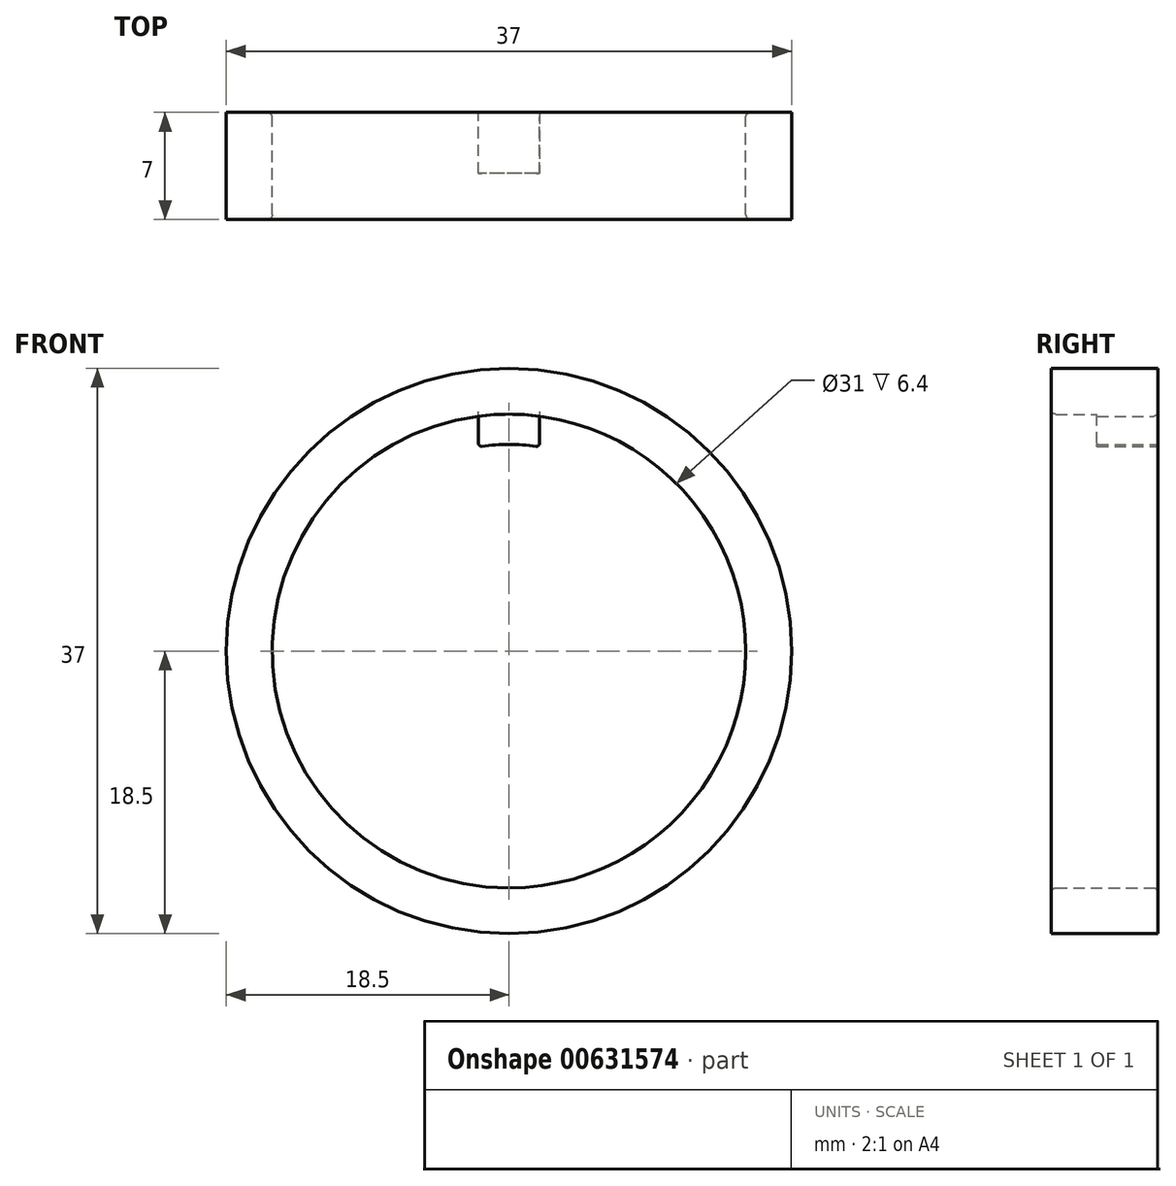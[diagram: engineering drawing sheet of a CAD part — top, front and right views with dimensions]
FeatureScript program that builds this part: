
annotation { "Feature Type Name" : "Feature", "Feature Type Description" : "" }
export const myFeature = defineFeature(function(context is Context, id is Id, definition is map)
    precondition{}
    {
        {
            var Q0;
            Q0=qCreatedBy(makeId("Front.planeOp"),FACE);
            var sketch = newSketch(context, id + "F0", { "sketchPlane" : qUnion([Q0])});
            skCircle(sketch, "E0", {"center": v(0, 0) * mm, "radius": 18.5 * mm});
            skCircle(sketch, "E1", {"center": v(0, 0) * mm, "radius": 15.5 * mm});
            skSolve(sketch);
        }
        {
            var Q0;
            Q0=makeQuery(id+"F0.imprint","IMPRINT",FACE,{"disambiguationData":[TD([[makeQuery(id+"F0.imprint","IMPRINT",EDGE,{"derivedFrom":sQuery(id+"F0.wireOp",EDGE,"E0")}),1.0]])]});
            extrude(context, id + "F1", {"entities" : qUnion([Q0]), "depth" : 7 * mm, "offsetDistance" : 25 * mm});
        }
        {
            var Q0;
            Q0=qCreatedBy(makeId("Front.planeOp"),FACE);
            var sketch = newSketch(context, id + "F2", { "sketchPlane" : qUnion([Q0])});
            skLineSegment(sketch, "E2", {"start": v(2, 13.37) * mm, "end": v(2, 15.37) * mm});
            skLineSegment(sketch, "E3.MirrorCS", {"start": v(-2, 13.37) * mm, "end": v(-2, 15.37) * mm});
            skArc(sketch, "E4", {"start": v(2, 15.37) * mm, "mid": v(0, 15.5) * mm, "end": v(-2, 15.37) * mm});
            skArc(sketch, "E5", {"start": v(2, 13.37) * mm, "mid": v(0, 13.52) * mm, "end": v(-2, 13.37) * mm});
            skLineSegment(sketch, "E6", {"start": v(0, -15.6) * mm, "end": v(0, 15.5) * mm, "construction": true});
            skSolve(sketch);
        }
        {
            var Q0;
            Q0 = qSketchRegion(id + "F2", true);
            extrude(context, id + "F3", {"entities" : qUnion([Q0]), "operationType" : NewBodyOperationType.ADD, "depth" : 4 * mm, "offsetDistance" : 25 * mm});
        }
        {
            var Q0;
            Q0=makeQuery(id+"F3.opExtrude","SWEPT_EDGE",EDGE,{"disambiguationData":[OSD([sQuery(id+"F2.wireOp",EDGE,"E2"),sQuery(id+"F2.wireOp",EDGE,"E5")])]});
            var Q1;
            Q1=makeQuery(id+"F3.opExtrude","SWEPT_EDGE",EDGE,{"disambiguationData":[OSD([sQuery(id+"F2.wireOp",EDGE,"E3.MirrorCS"),sQuery(id+"F2.wireOp",EDGE,"E5")])]});
            fillet(context, id + "F4", {"entities" : qUnion([Q0, Q1]), "radius" : .2 * mm, "tangentPropagation" : true, "allowEdgeOverflow" : false});
        }
        {
            var Q0;
            Q0=makeQuery(id+"F1.opExtrude","CAP_EDGE",EDGE,{"disambiguationData":[OSD([sQuery(id+"F0.wireOp",EDGE,"E1")])],"isStart":false});
            var Q1;
            {var subQ2=sQuery(id+"F2.wireOp",EDGE,"E3.MirrorCS");var subQ4=sQuery(id+"F0.wireOp",EDGE,"E1");Q1=makeQuery(id+"FiiVZIjtQJF6cDl_1.1.F3.boolean.opBoolean","SPLIT",EDGE,{"disambiguationData":[TD([makeQuery(id+"F3.opExtrude","SWEPT_FACE",FACE,{"disambiguationData":[OSD([subQ2])]})])],"derivedFrom":makeQuery(id+"F1.opExtrude","CAP_EDGE",EDGE,{"disambiguationData":[OSD([subQ4])],"isStart":true})});}
            var Q2;
            {var subQ3=sQuery(id+"F2.wireOp",EDGE,"E2");var subQ5=makeQuery(id+"F3.opExtrude","SWEPT_FACE",FACE,{"disambiguationData":[OSD([subQ3])]});var subQ6=sQuery(id+"F0.wireOp",EDGE,"E1");Q2=makeQuery(id+"FiiVZIjtQJF6cDl_1.3.F3.boolean.opBoolean","SPLIT",EDGE,{"disambiguationData":[TD([subQ5])],"derivedFrom":makeQuery(id+"FiiVZIjtQJF6cDl_1.2.F3.boolean.opBoolean","SPLIT",EDGE,{"disambiguationData":[TD([subQ5])],"derivedFrom":makeQuery(id+"FiiVZIjtQJF6cDl_1.1.F3.boolean.opBoolean","SPLIT",EDGE,{"disambiguationData":[TD([subQ5])],"derivedFrom":makeQuery(id+"F1.opExtrude","CAP_EDGE",EDGE,{"disambiguationData":[OSD([subQ6])],"isStart":true})})})});}
            var Q3;
            {var subQ2=sQuery(id+"F2.wireOp",EDGE,"E3.MirrorCS");var subQ3=sQuery(id+"F2.wireOp",EDGE,"E2");var subQ5=sQuery(id+"F0.wireOp",EDGE,"E1");var subQ10=makeQuery(id+"FiiVZIjtQJF6cDl_1.2.F3.opExtrude","SWEPT_FACE",FACE,{"disambiguationData":[OSD([subQ2])]});var subQ11=makeQuery(id+"F3.opExtrude","SWEPT_FACE",FACE,{"disambiguationData":[OSD([subQ3])]});Q3=makeQuery(id+"FiiVZIjtQJF6cDl_1.3.F3.boolean.opBoolean","SPLIT",EDGE,{"disambiguationData":[TD([subQ10])],"derivedFrom":makeQuery(id+"FiiVZIjtQJF6cDl_1.2.F3.boolean.opBoolean","SPLIT",EDGE,{"disambiguationData":[TD([subQ11])],"derivedFrom":makeQuery(id+"FiiVZIjtQJF6cDl_1.1.F3.boolean.opBoolean","SPLIT",EDGE,{"disambiguationData":[TD([subQ11])],"derivedFrom":makeQuery(id+"F1.opExtrude","CAP_EDGE",EDGE,{"disambiguationData":[OSD([subQ5])],"isStart":true})})})});}
            var Q4;
            {var subQ2=sQuery(id+"F2.wireOp",EDGE,"E3.MirrorCS");var subQ3=sQuery(id+"F2.wireOp",EDGE,"E2");var subQ5=sQuery(id+"F0.wireOp",EDGE,"E1");var subQ9=makeQuery(id+"FiiVZIjtQJF6cDl_1.1.F3.opExtrude","SWEPT_FACE",FACE,{"disambiguationData":[OSD([subQ2])]});Q4=makeQuery(id+"FiiVZIjtQJF6cDl_1.2.F3.boolean.opBoolean","SPLIT",EDGE,{"disambiguationData":[TD([subQ9])],"derivedFrom":makeQuery(id+"FiiVZIjtQJF6cDl_1.1.F3.boolean.opBoolean","SPLIT",EDGE,{"disambiguationData":[TD([makeQuery(id+"F3.opExtrude","SWEPT_FACE",FACE,{"disambiguationData":[OSD([subQ3])]})])],"derivedFrom":makeQuery(id+"F1.opExtrude","CAP_EDGE",EDGE,{"disambiguationData":[OSD([subQ5])],"isStart":true})})});}
            fillet(context, id + "F5", {"entities" : qUnion([Q0, Q1, Q2, Q3, Q4]), "radius" : .3 * mm, "tangentPropagation" : true, "allowEdgeOverflow" : false});
        }
    });
